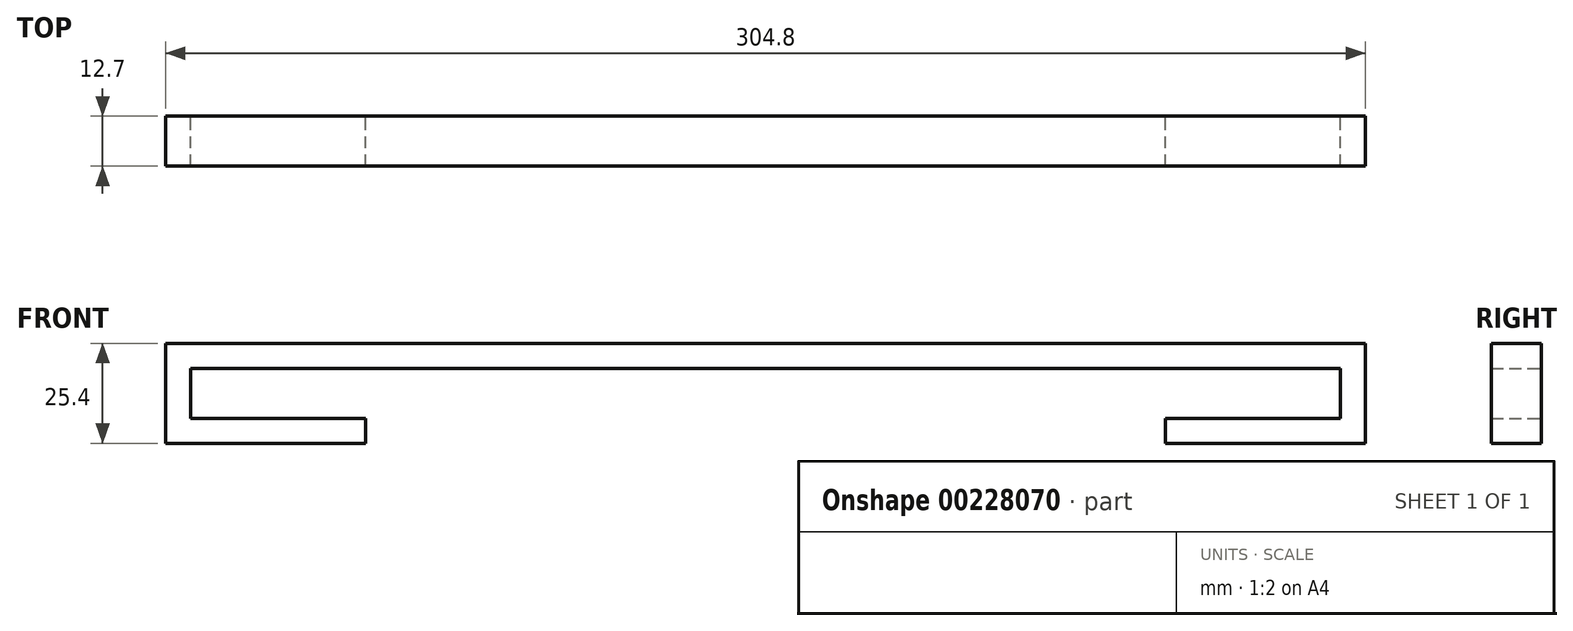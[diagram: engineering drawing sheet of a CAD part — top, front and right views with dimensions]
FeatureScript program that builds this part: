
annotation { "Feature Type Name" : "Feature", "Feature Type Description" : "" }
export const myFeature = defineFeature(function(context is Context, id is Id, definition is map)
    precondition{}
    {
        {
            var Q0;
            Q0=qCreatedBy(makeId("Front.planeOp"),FACE);
            var sketch = newSketch(context, id + "F0", { "sketchPlane" : qUnion([Q0])});
            skLineSegment(sketch, "E0", {"start": v(0, 0) * mm, "end": v(0, 25.4) * mm});
            skLineSegment(sketch, "E1", {"start": v(0, 25.4) * mm, "end": v(304.8, 25.4) * mm});
            skLineSegment(sketch, "E2", {"start": v(304.8, 25.4) * mm, "end": v(304.8, 0) * mm});
            skLineSegment(sketch, "E3", {"start": v(304.8, 0) * mm, "end": v(254, 0) * mm});
            skLineSegment(sketch, "E4", {"start": v(298.45, 19.05) * mm, "end": v(6.35, 19.05) * mm});
            skLineSegment(sketch, "E5", {"start": v(50.8, 0) * mm, "end": v(0, 0) * mm});
            skLineSegment(sketch, "E6", {"start": v(50.8, 0) * mm, "end": v(50.8, 6.35) * mm});
            skLineSegment(sketch, "E7", {"start": v(50.8, 6.35) * mm, "end": v(6.35, 6.35) * mm});
            skLineSegment(sketch, "E8", {"start": v(6.35, 6.35) * mm, "end": v(6.35, 19.05) * mm});
            skLineSegment(sketch, "E9", {"start": v(254, 0) * mm, "end": v(254, 6.35) * mm});
            skLineSegment(sketch, "E10", {"start": v(254, 6.35) * mm, "end": v(298.45, 6.35) * mm});
            skLineSegment(sketch, "E11", {"start": v(298.45, 6.35) * mm, "end": v(298.45, 19.05) * mm});
            skSolve(sketch);
        }
        {
            var Q0;
            Q0 = qSketchRegion(id + "F0", true);
            extrude(context, id + "F1", {"entities" : qUnion([Q0]), "depth" : 12.7 * mm});
        }
    });
